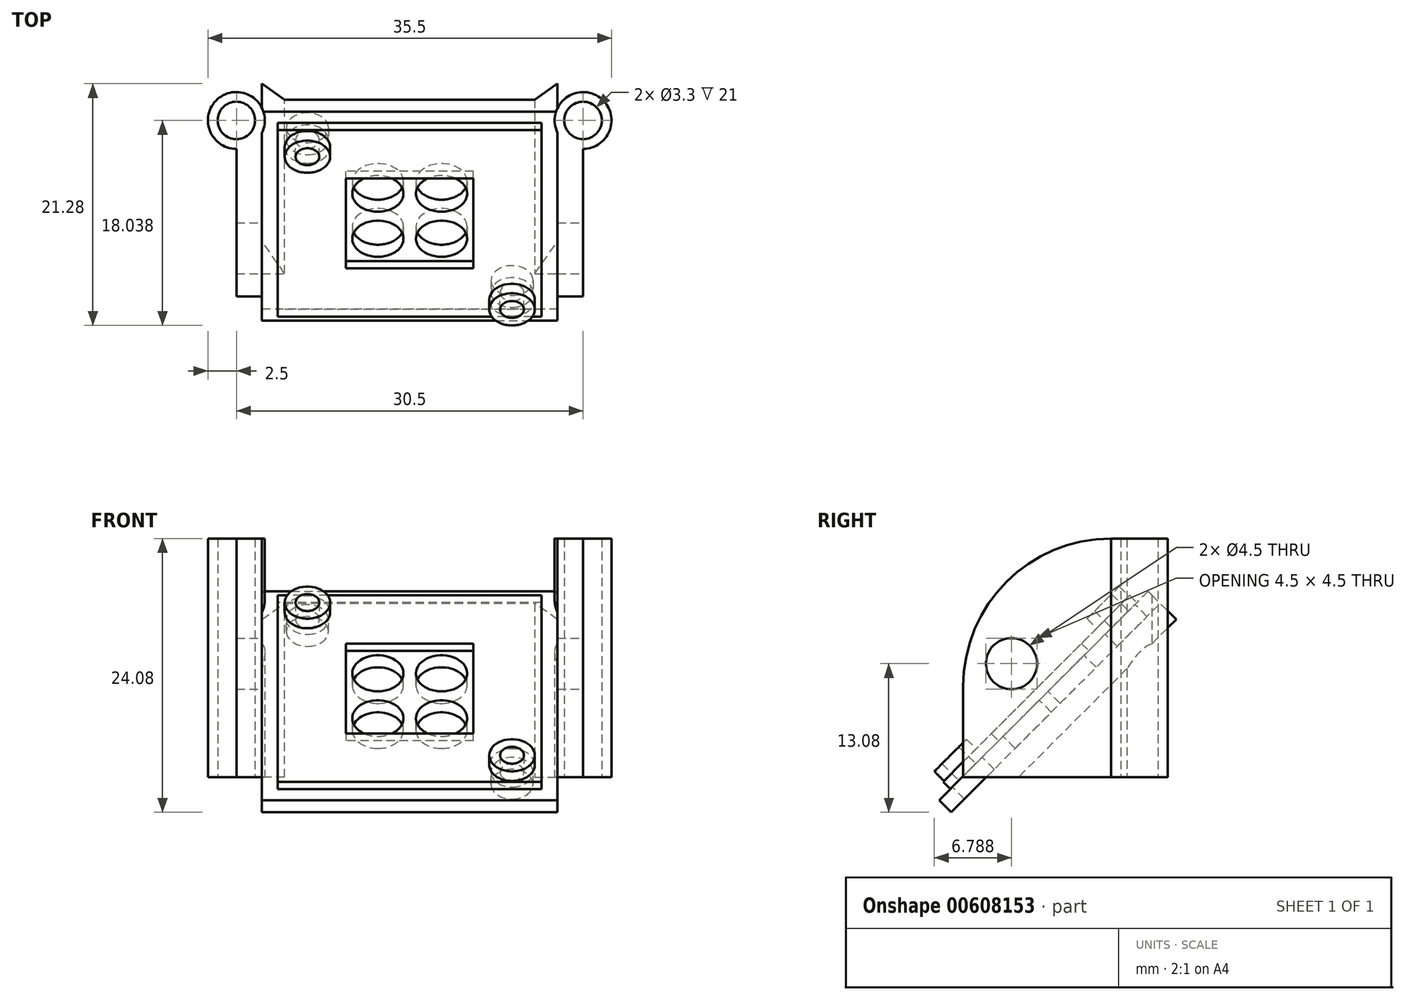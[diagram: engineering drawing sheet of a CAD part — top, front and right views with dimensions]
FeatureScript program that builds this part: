
annotation { "Feature Type Name" : "Feature", "Feature Type Description" : "" }
export const myFeature = defineFeature(function(context is Context, id is Id, definition is map)
    precondition{}
    {
        {
            var Q0;
            Q0=qCreatedBy(makeId("Top.planeOp"),FACE);
            var sketch = newSketch(context, id + "F0", { "sketchPlane" : qUnion([Q0])});
            skLineSegment(sketch, "E0", {"start": v(15.25, 24.62) * mm, "end": v(-15.25, 24.62) * mm, "construction": true});
            skCircle(sketch, "E1", {"center": v(-15.25, 24.62) * mm, "radius": 1.65 * mm});
            skCircle(sketch, "E2", {"center": v(-15.25, 24.62) * mm, "radius": 2.5 * mm});
            skCircle(sketch, "E3", {"center": v(15.25, 24.62) * mm, "radius": 1.65 * mm});
            skCircle(sketch, "E4", {"center": v(15.25, 24.62) * mm, "radius": 2.5 * mm});
            skPoint(sketch, "E5", {"position": v(-15.25, 22.12) * mm});
            skLineSegment(sketch, "E6", {"start": v(-15.25, 24.62) * mm, "end": v(-15.25, 9.12) * mm, "construction": true});
            skLineSegment(sketch, "E7", {"start": v(-15.25, 9.12) * mm, "end": v(15.25, 9.12) * mm, "construction": true});
            skLineSegment(sketch, "E8", {"start": v(15.25, 9.12) * mm, "end": v(15.25, 24.62) * mm, "construction": true});
            skLineSegment(sketch, "E9", {"start": v(15.25, 22.12) * mm, "end": v(15.25, 9.12) * mm});
            skLineSegment(sketch, "E10", {"start": v(15.25, 9.12) * mm, "end": v(13, 9.12) * mm});
            skLineSegment(sketch, "E11", {"start": v(13, 9.12) * mm, "end": v(13, 23.53) * mm});
            skLineSegment(sketch, "E12", {"start": v(-15.25, 22.12) * mm, "end": v(-15.25, 9.12) * mm});
            skLineSegment(sketch, "E13", {"start": v(-15.25, 9.12) * mm, "end": v(-13, 9.12) * mm});
            skLineSegment(sketch, "E14", {"start": v(-13, 9.12) * mm, "end": v(-13, 23.53) * mm});
            skSolve(sketch);
        }
        {
            var Q0;
            Q0=makeQuery(id+"F0.imprint","IMPRINT",FACE,{"disambiguationData":[TD([[makeQuery(id+"F0.imprint","IMPRINT",EDGE,{"derivedFrom":sQuery(id+"F0.wireOp",EDGE,"E1")}),-1.0]])]});
            var Q1;
            Q1=makeQuery(id+"F0.imprint","IMPRINT",FACE,{"disambiguationData":[TD([[makeQuery(id+"F0.imprint","IMPRINT",EDGE,{"derivedFrom":sQuery(id+"F0.wireOp",EDGE,"E3")}),-1.0]])]});
            var Q2;
            Q2=makeQuery(id+"F0.imprint","IMPRINT",FACE,{"disambiguationData":[TD([[makeQuery(id+"F0.imprint","IMPRINT",EDGE,{"derivedFrom":sQuery(id+"F0.wireOp",EDGE,"GyxC4Cwi-RMFc-qVmH-YboR-WA0SqB4U5H94")}),-1.0]])]});
            var Q3;
            Q3=makeQuery(id+"F0.imprint","IMPRINT",FACE,{"disambiguationData":[TD([[makeQuery(id+"F0.imprint","IMPRINT",EDGE,{"derivedFrom":sQuery(id+"F0.wireOp",EDGE,"82AeB47f-6y09-gEI0-IFZB-KstoD60AnrTl")}),-1.0]])]});
            var Q4;
            {var subQ0=sQuery(id+"F0.wireOp",EDGE,"E9");Q4=makeQuery(id+"F0.imprint","IMPRINT",FACE,{"disambiguationData":[TD([[makeQuery(id+"F0.imprint","IMPRINT",EDGE,{"derivedFrom":subQ0}),-1.0]])]});}
            var Q5;
            {var subQ0=sQuery(id+"F0.wireOp",EDGE,"E12");Q5=makeQuery(id+"F0.imprint","IMPRINT",FACE,{"disambiguationData":[TD([[makeQuery(id+"F0.imprint","IMPRINT",EDGE,{"derivedFrom":subQ0}),1.0]])]});}
            extrude(context, id + "F1", {"entities" : qUnion([Q0, Q1, Q2, Q3, Q4, Q5]), "depth" : 21 * mm, "offsetDistance" : 25 * mm});
        }
        {
            var Q0;
            Q0=makeQuery(id+"F1.opExtrude","CAP_EDGE",EDGE,{"disambiguationData":[OSD([sQuery(id+"F0.wireOp",EDGE,"E13")])],"isStart":false});
            var Q1;
            Q1=makeQuery(id+"F1.opExtrude","CAP_EDGE",EDGE,{"disambiguationData":[OSD([sQuery(id+"F0.wireOp",EDGE,"E10")])],"isStart":false});
            fillet(context, id + "F2", {"entities" : qUnion([Q0, Q1]), "radius" : 13 * mm, "tangentPropagation" : true, "allowEdgeOverflow" : false});
        }
        {
            var Q0;
            Q0=makeQuery(id+"F1.opExtrude","SWEPT_FACE",FACE,{"disambiguationData":[OSD([sQuery(id+"F0.wireOp",EDGE,"E9")])]});
            var sketch = newSketch(context, id + "F3", { "sketchPlane" : qUnion([Q0])});
            skLineSegment(sketch, "E15", {"start": v(9.12, 0) * mm, "end": v(13.37, 0) * mm, "construction": true});
            skLineSegment(sketch, "E16", {"start": v(13.37, 0) * mm, "end": v(13.37, 10) * mm, "construction": true});
            skCircle(sketch, "E17", {"center": v(13.37, 10) * mm, "radius": 2.25 * mm});
            skSolve(sketch);
        }
        {
            var Q0;
            Q0=sQuery(id+"F3.wireOp",VERTEX,"E17.center");
            var Q1;
            Q1=makeQuery(id+"F1.opExtrude","SWEPT_BODY",BODY,{"disambiguationData":[OSD([sQuery(id+"F0.wireOp",EDGE,"E1"),sQuery(id+"F0.wireOp",EDGE,"E2"),sQuery(id+"F0.wireOp",EDGE,"E12"),sQuery(id+"F0.wireOp",EDGE,"E13"),sQuery(id+"F0.wireOp",EDGE,"E14")])]});
            var Q2;
            Q2=makeQuery(id+"F1.opExtrude","SWEPT_BODY",BODY,{"disambiguationData":[OSD([sQuery(id+"F0.wireOp",EDGE,"E3"),sQuery(id+"F0.wireOp",EDGE,"E4"),sQuery(id+"F0.wireOp",EDGE,"E9"),sQuery(id+"F0.wireOp",EDGE,"E10"),sQuery(id+"F0.wireOp",EDGE,"E11")])]});
            hole(context, id + "F4", {"style" : HoleStyle.SIMPLE, "endStyle" : HoleEndStyle.THROUGH, "holeDiameter" : 4.5 * mm, "isTappedThrough" : true, "tappedDepth" : 12 * mm, "tapClearance" : 3, "locations" : qUnion([Q0]), "scope" : qUnion([Q1, Q2])});
        }
        {
            var Q0;
            Q0=makeQuery(id+"F1.opExtrude","SWEPT_FACE",FACE,{"disambiguationData":[OSD([sQuery(id+"F0.wireOp",EDGE,"E11")])]});
            var sketch = newSketch(context, id + "F5", { "sketchPlane" : qUnion([Q0])});
            skLineSegment(sketch, "E18", {"start": v(-13.37, 10) * mm, "end": v(-13.37, 0) * mm, "construction": true});
            skLineSegment(sketch, "E19", {"start": v(-13.37, 0) * mm, "end": v(-13.37, 10) * mm, "construction": true});
            skLineSegment(sketch, "E20", {"start": v(-13.37, 10) * mm, "end": v(-16.2, 7.17) * mm, "construction": true});
            skLineSegment(sketch, "E21", {"start": v(-16.2, 7.17) * mm, "end": v(-25.39, 16.36) * mm});
            skLineSegment(sketch, "E22", {"start": v(-25.39, 16.36) * mm, "end": v(-26.45, 15.3) * mm});
            skLineSegment(sketch, "E23", {"start": v(-26.45, 15.3) * mm, "end": v(-8.06, -3.08) * mm});
            skLineSegment(sketch, "E24", {"start": v(-8.06, -3.08) * mm, "end": v(-7, -2.02) * mm});
            skLineSegment(sketch, "E25", {"start": v(-7, -2.02) * mm, "end": v(-16.2, 7.17) * mm});
            skSolve(sketch);
        }
        {
            var Q0;
            {var subQ0=sQuery(id+"F5.wireOp",EDGE,"E25");var subQ1=sQuery(id+"F5.wireOp",EDGE,"E21");var subQ2=makeQuery(id+"F5.imprint","INTERSECT",VERTEX,{"derivedFrom":[subQ1,subQ0]});Q0=makeQuery(id+"F5.imprint","IMPRINT",FACE,{"disambiguationData":[TD([[makeQuery(id+"F5.imprint","IMPRINT",EDGE,{"disambiguationData":[TD([[subQ2,-1.0]])],"derivedFrom":subQ1}),1.0]])]});}
            var Q1;
            {var subQ0=sQuery(id+"F5.wireOp",EDGE,"E22");Q1=makeQuery(id+"F5.imprint","IMPRINT",FACE,{"disambiguationData":[TD([[makeQuery(id+"F5.imprint","IMPRINT",EDGE,{"derivedFrom":subQ0}),1.0]])]});}
            var Q2;
            {var subQ1=sQuery(id+"F5.wireOp",EDGE,"E24");Q2=makeQuery(id+"F5.imprint","IMPRINT",FACE,{"disambiguationData":[TD([[makeQuery(id+"F5.imprint","IMPRINT",EDGE,{"derivedFrom":subQ1}),1.0]])]});}
            extrude(context, id + "F6", {"entities" : qUnion([Q0, Q1, Q2]), "depth" : 26 * mm, "offsetDistance" : 25 * mm});
        }
        {
            var Q0;
            Q0=makeQuery(id+"F6.opExtrude","SWEPT_FACE",FACE,{"disambiguationData":[OSD([sQuery(id+"F5.wireOp",EDGE,"E21"),sQuery(id+"F5.wireOp",EDGE,"E25")])]});
            var sketch = newSketch(context, id + "F7", { "sketchPlane" : qUnion([Q0])});
            skLineSegment(sketch, "E26", {"start": v(-13, 29.52) * mm, "end": v(-9, 29.52) * mm, "construction": true});
            skLineSegment(sketch, "E27", {"start": v(-9, 29.52) * mm, "end": v(-9, 26.02) * mm, "construction": true});
            skLineSegment(sketch, "E28", {"start": v(13, 3.52) * mm, "end": v(9, 3.52) * mm, "construction": true});
            skLineSegment(sketch, "E29", {"start": v(9, 3.52) * mm, "end": v(9, 7.02) * mm, "construction": true});
            skPoint(sketch, "E30.endSnap0", {"position": v(0, 3.52) * mm});
            skLineSegment(sketch, "E31.bottom", {"start": v(11.6, 4.92) * mm, "end": v(-11.6, 4.92) * mm});
            skLineSegment(sketch, "E31.top", {"start": v(11.6, 28.12) * mm, "end": v(-11.6, 28.12) * mm});
            skLineSegment(sketch, "E31.left", {"start": v(11.6, 4.92) * mm, "end": v(11.6, 28.12) * mm});
            skLineSegment(sketch, "E31.right", {"start": v(-11.6, 4.92) * mm, "end": v(-11.6, 28.12) * mm});
            skPoint(sketch, "E31.middle", {"position": v(0, 16.52) * mm});
            skLineSegment(sketch, "E32.bottom", {"start": v(5.6, 10.92) * mm, "end": v(-5.6, 10.92) * mm});
            skLineSegment(sketch, "E32.top", {"start": v(5.6, 22.12) * mm, "end": v(-5.6, 22.12) * mm});
            skLineSegment(sketch, "E32.left", {"start": v(5.6, 10.92) * mm, "end": v(5.6, 22.12) * mm});
            skLineSegment(sketch, "E32.right", {"start": v(-5.6, 10.92) * mm, "end": v(-5.6, 22.12) * mm});
            skCircle(sketch, "E33", {"center": v(-9, 26.02) * mm, "radius": 1.05 * mm});
            skCircle(sketch, "E34", {"center": v(9, 7.02) * mm, "radius": 1.05 * mm});
            skCircle(sketch, "E35", {"center": v(9, 7.02) * mm, "radius": 2 * mm});
            skCircle(sketch, "E36", {"center": v(-9, 26.02) * mm, "radius": 2 * mm});
            skCircle(sketch, "E37", {"center": v(9, 7.02) * mm, "radius": 1.8 * mm, "construction": true});
            skCircle(sketch, "E38", {"center": v(-9, 26.02) * mm, "radius": 1.8 * mm, "construction": true});
            skLineSegment(sketch, "E39", {"start": v(0, 16.52) * mm, "end": v(-5.6, 16.52) * mm, "construction": true});
            skLineSegment(sketch, "E40", {"start": v(-2.8, 16.52) * mm, "end": v(-2.8, 22.12) * mm, "construction": true});
            skLineSegment(sketch, "E41", {"start": v(-2.8, 16.52) * mm, "end": v(-2.8, 10.92) * mm, "construction": true});
            skLineSegment(sketch, "E42", {"start": v(0, 16.52) * mm, "end": v(5.6, 16.52) * mm, "construction": true});
            skLineSegment(sketch, "E43", {"start": v(2.8, 16.52) * mm, "end": v(2.8, 22.12) * mm, "construction": true});
            skLineSegment(sketch, "E44", {"start": v(2.8, 16.52) * mm, "end": v(2.8, 10.92) * mm, "construction": true});
            skLineSegment(sketch, "E45", {"start": v(2.8, 13.72) * mm, "end": v(-2.8, 13.72) * mm, "construction": true});
            skLineSegment(sketch, "E46", {"start": v(-2.8, 13.72) * mm, "end": v(-2.8, 19.32) * mm, "construction": true});
            skLineSegment(sketch, "E47", {"start": v(-2.8, 19.32) * mm, "end": v(2.8, 19.32) * mm, "construction": true});
            skCircle(sketch, "E48", {"center": v(-2.8, 19.32) * mm, "radius": 2.25 * mm, "construction": true});
            skCircle(sketch, "E49", {"center": v(2.8, 19.32) * mm, "radius": 2.25 * mm, "construction": true});
            skCircle(sketch, "E50", {"center": v(2.8, 13.72) * mm, "radius": 2.25 * mm, "construction": true});
            skCircle(sketch, "E51", {"center": v(-2.8, 13.72) * mm, "radius": 2.25 * mm, "construction": true});
            skSolve(sketch);
        }
        {
            var Q0;
            Q0=sQuery(id+"F7.wireOp",VERTEX,"xRpNI7OB-sENC-NIWt-IonO-ULPQCYI2OJvv.center");
            var Q1;
            Q1=sQuery(id+"F7.wireOp",VERTEX,"aurLsu0g-ZDsF-CTWi-w7Pd-vwTeFcaxKEEF.center");
            var Q2;
            Q2=sQuery(id+"F7.wireOp",VERTEX,"E33.center");
            var Q3;
            Q3=sQuery(id+"F7.wireOp",VERTEX,"E29.end");
            var Q4;
            Q4=makeQuery(id+"F6.opExtrude","SWEPT_BODY",BODY,{"disambiguationData":[OSD([sQuery(id+"F5.wireOp",EDGE,"E21"),sQuery(id+"F5.wireOp",EDGE,"E22"),sQuery(id+"F5.wireOp",EDGE,"E23"),sQuery(id+"F5.wireOp",EDGE,"E24"),sQuery(id+"F5.wireOp",EDGE,"E25")])]});
            hole(context, id + "F8", {"style" : HoleStyle.SIMPLE, "endStyle" : HoleEndStyle.THROUGH, "holeDiameter" : 3.7 * mm, "isTappedThrough" : true, "tappedDepth" : 12 * mm, "tapClearance" : 3, "locations" : qUnion([Q0, Q1, Q2, Q3]), "scope" : qUnion([Q4])});
        }
        {
            var Q0;
            Q0=makeQuery(id+"F7.imprint","IMPRINT",FACE,{"disambiguationData":[TD([[makeQuery(id+"F7.imprint","IMPRINT",EDGE,{"derivedFrom":sQuery(id+"F7.wireOp",EDGE,"E31.bottom")}),-1.0]])]});
            extrude(context, id + "F9", {"entities" : qUnion([Q0]), "operationType" : NewBodyOperationType.ADD, "depth" : 0.9 * mm, "offsetDistance" : 25 * mm});
        }
        {
            var Q0;
            Q0=makeQuery(id+"F7.imprint","IMPRINT",FACE,{"disambiguationData":[TD([[makeQuery(id+"F7.imprint","IMPRINT",EDGE,{"derivedFrom":sQuery(id+"F7.wireOp",EDGE,"E33")}),-1.0]])]});
            var Q1;
            Q1=makeQuery(id+"F7.imprint","IMPRINT",FACE,{"disambiguationData":[TD([[makeQuery(id+"F7.imprint","IMPRINT",EDGE,{"derivedFrom":sQuery(id+"F7.wireOp",EDGE,"E34")}),-1.0]])]});
            extrude(context, id + "F10", {"entities" : qUnion([Q0, Q1]), "operationType" : NewBodyOperationType.ADD, "depth" : 2.1 * mm, "offsetDistance" : 25 * mm});
        }
        {
            var Q0;
            Q0=sQuery(id+"F7.wireOp",VERTEX,"E46.end");
            var Q1;
            Q1=sQuery(id+"F7.wireOp",VERTEX,"E47.end");
            var Q2;
            Q2=sQuery(id+"F7.wireOp",VERTEX,"E45.start");
            var Q3;
            Q3=sQuery(id+"F7.wireOp",VERTEX,"E46.start");
            var Q4;
            Q4=makeQuery(id+"F6.opExtrude","SWEPT_BODY",BODY,{"disambiguationData":[OSD([sQuery(id+"F5.wireOp",EDGE,"E21"),sQuery(id+"F5.wireOp",EDGE,"E22"),sQuery(id+"F5.wireOp",EDGE,"E23"),sQuery(id+"F5.wireOp",EDGE,"E24"),sQuery(id+"F5.wireOp",EDGE,"E25")])]});
            hole(context, id + "F11", {"style" : HoleStyle.SIMPLE, "endStyle" : HoleEndStyle.THROUGH, "holeDiameter" : 4.5 * mm, "isTappedThrough" : true, "tappedDepth" : 12 * mm, "tapClearance" : 3, "locations" : qUnion([Q0, Q1, Q2, Q3]), "scope" : qUnion([Q4])});
        }
        {
            var Q0;
            Q0=makeQuery(id+"F1.opExtrude","SWEPT_BODY",BODY,{"disambiguationData":[OSD([sQuery(id+"F0.wireOp",EDGE,"E1"),sQuery(id+"F0.wireOp",EDGE,"E2"),sQuery(id+"F0.wireOp",EDGE,"E12"),sQuery(id+"F0.wireOp",EDGE,"E13"),sQuery(id+"F0.wireOp",EDGE,"E14")])]});
            var Q1;
            Q1=makeQuery(id+"F1.opExtrude","SWEPT_BODY",BODY,{"disambiguationData":[OSD([sQuery(id+"F0.wireOp",EDGE,"E3"),sQuery(id+"F0.wireOp",EDGE,"E4"),sQuery(id+"F0.wireOp",EDGE,"E9"),sQuery(id+"F0.wireOp",EDGE,"E10"),sQuery(id+"F0.wireOp",EDGE,"E11")])]});
            var Q2;
            Q2=makeQuery(id+"F6.opExtrude","SWEPT_BODY",BODY,{"disambiguationData":[OSD([sQuery(id+"F5.wireOp",EDGE,"E21"),sQuery(id+"F5.wireOp",EDGE,"E22"),sQuery(id+"F5.wireOp",EDGE,"E23"),sQuery(id+"F5.wireOp",EDGE,"E24"),sQuery(id+"F5.wireOp",EDGE,"E25")])]});
            booleanBodies(context, id + "F12", {"operationType" : BooleanOperationType.UNION, "tools" : qUnion([Q0, Q1, Q2])});
        }
        {
            var Q0;
            {var subQ0=sQuery(id+"F5.wireOp",EDGE,"E23");Q0=makeQuery(id+"F12.opBoolean","SPLIT",EDGE,{"disambiguationData":[topologyDisambiguationEdgeConnected([makeQuery(id+"F1.opExtrude","SWEPT_FACE",FACE,{"disambiguationData":[OSD([sQuery(id+"F0.wireOp",EDGE,"E11")])]}),makeQuery(id+"F6.opExtrude","SWEPT_FACE",FACE,{"disambiguationData":[OSD([subQ0])]})])],"derivedFrom":makeQuery(id+"F6.opExtrude","CAP_EDGE",EDGE,{"disambiguationData":[OSD([subQ0])],"isStart":true})});}
            var Q1;
            {var subQ0=sQuery(id+"F5.wireOp",EDGE,"E23");Q1=makeQuery(id+"F12.opBoolean","SPLIT",EDGE,{"disambiguationData":[topologyDisambiguationEdgeConnected([makeQuery(id+"F1.opExtrude","SWEPT_FACE",FACE,{"disambiguationData":[OSD([sQuery(id+"F0.wireOp",EDGE,"E14")])]}),makeQuery(id+"F6.opExtrude","SWEPT_FACE",FACE,{"disambiguationData":[OSD([subQ0])]})])],"derivedFrom":makeQuery(id+"F6.opExtrude","CAP_EDGE",EDGE,{"disambiguationData":[OSD([subQ0])],"isStart":false})});}
            chamfer(context, id + "F13", {"entities" : qUnion([Q0, Q1]), "width" : 2 * mm, "tangentPropagation" : true});
        }
    });
